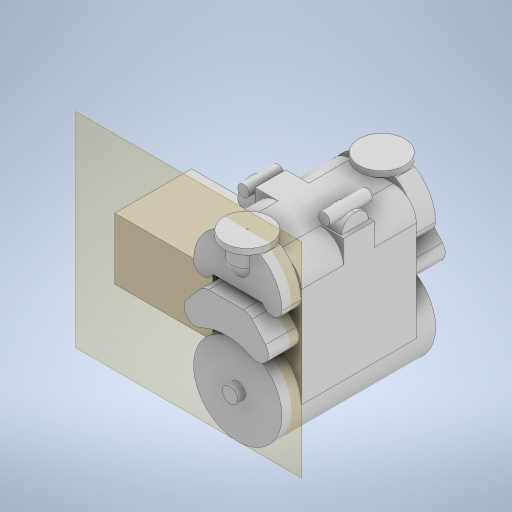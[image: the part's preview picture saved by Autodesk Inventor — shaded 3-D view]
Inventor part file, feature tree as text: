
AUTODESK INVENTOR PART (.ipt)
format: ipt  version: 2023 (Build 270158000, 158)  size: 474,624 bytes
history: native  units: in
note: dims shown in document units (in); Inventor stores cm internally (conversion verified against a paired STEP export)
features: extrude x12, sketch x12, plane x2, revolve x1, mirror x1, other x1
ambient origin geometry x8: Origin, YZ Plane, XZ Plane, XY Plane, X Axis, Y Axis, Z Axis, Center Point
bodies: Solid1 (feature_tree)
feature tree (29):
  extrude  "Extrusion1"  Depth=23.0in
  extrude  "Extrusion2"  Depth=32.0in
  extrude  "Extrusion4"  Depth=12.5in
  extrude  "Extrusion5"  Depth=23.0in
  extrude  "Extrusion6"  Depth=5.0in
  extrude  "Extrusion7"  Depth=16.0in
  extrude  "Extrusion8"  Depth=9.0in
  plane  "Work Plane2"
  extrude  "Extrusion9"  Depth=5.0in
  plane  "Work Plane3"
  sketch  "Sketch16"  dims[d41=6.0in d42=0.0in d43=12.0in d44=1.5in d45=0.0in d46=4.0in d47=2.0in d48=0.0in d50=-1.0in d51=5.0in d52=0.0in d55=11.0in d56=0.0in d57=0.0in d58=0.5in d59=3.0in d60=0.0in d61=5.0in d62=0.0in d64=0.5in d65=3.0in d66=9.0in d67=0.0in d68=2.0in d69=14.0in d70=10.0in d71=10.0in d72=42.0in d73=0.0in d75=0.0in d76=4.0in d77=10.0in d78=90.0deg d74=0.5in]
  revolve  "Revolution2"  [1 undecoded]
  mirror  "Mirror3"
  extrude  "Extrusion10"  Depth=5.0in TaperAngle=0.0deg
  extrude  "Extrusion11"  Depth=4.0in
  extrude  "Extrusion12"  Depth=10.0in
  extrude  "Extrusion13"  Depth=1.5in TaperAngle=0.0deg
  sketch  "Sketch1"  dims[d0=23.0in d1=12.0in]
  sketch  "Sketch2"  dims[d2=12.0in d3=32.0in]
  sketch  "Sketch4"  dims[d4=15.0in d5=0.0in d6=12.5in]
  sketch  "Sketch5"  dims[d9=23.0in d10=23.0in]
  sketch  "Sketch6"  dims[d11=5.0in d12=0.0in d22=14.0in]
  sketch  "Sketch7"  dims[d23=3.0in d24=16.0in]
  sketch  "Sketch8"  dims[d25=22.0in d26=9.0in]
  sketch  "Sketch11"  dims[d27=8.0in d28=0.0in d29=5.0in]
  sketch  "Sketch12"  dims[d31=1.0in d32=1.0in]
  sketch  "Sketch13"  dims[d35=10.5in d36=5.0in d37=0.0in]
  sketch  "Sketch14"  dims[d38=4.0in d39=22.0in]
  other  "Work Point1"
note: 1 required parameter value undecoded (feature->parameter linkage not recoverable at this tier; creation-order binding heuristic only, values carry confidence <= 0.55)
